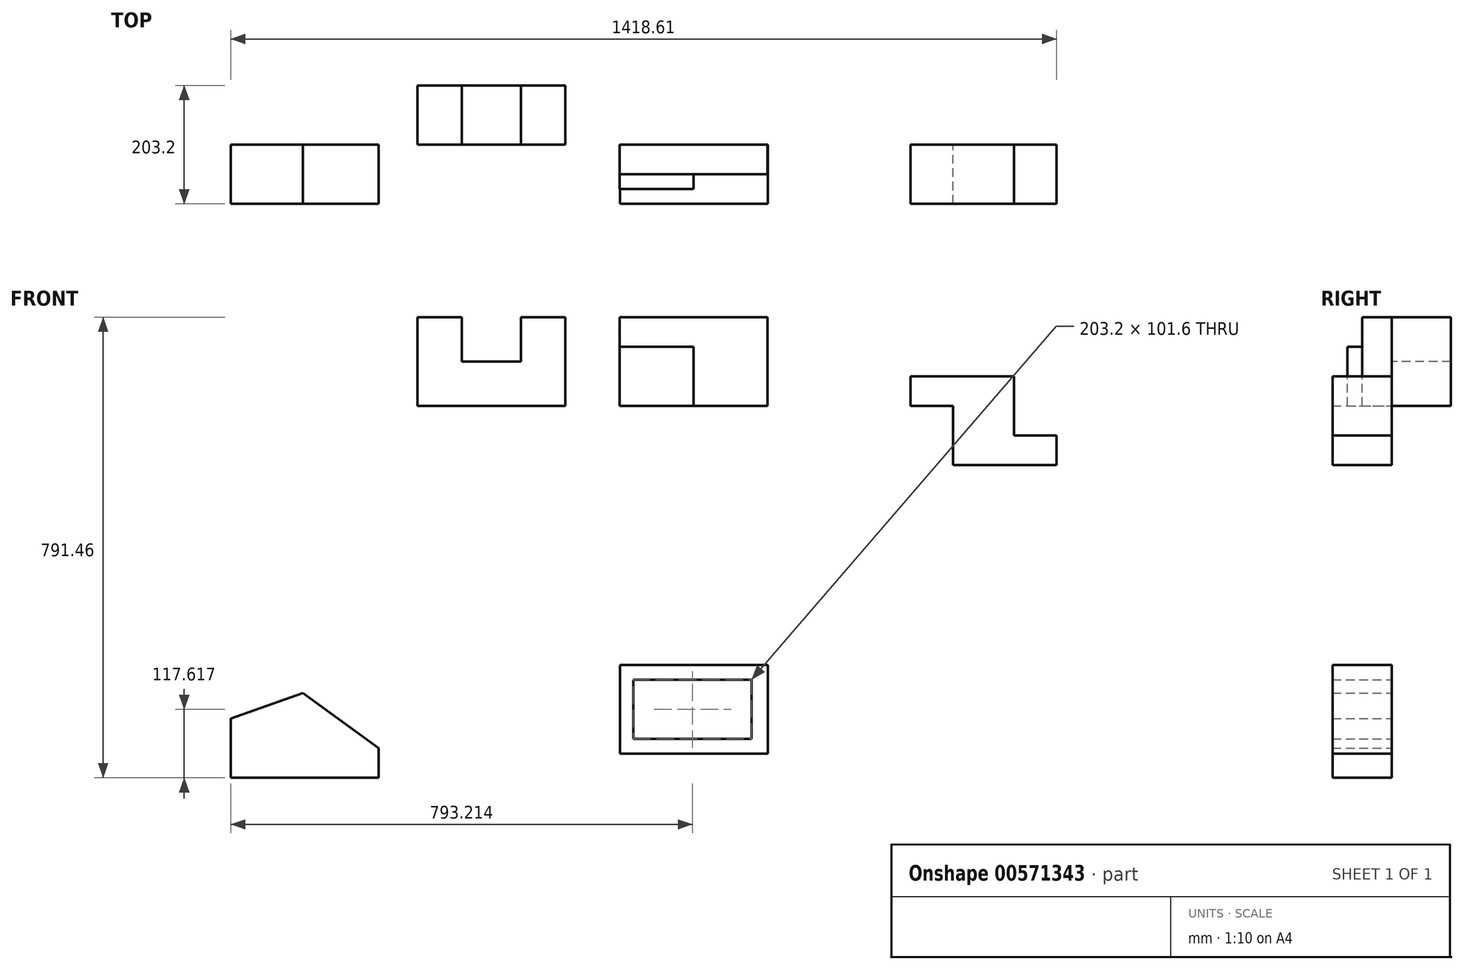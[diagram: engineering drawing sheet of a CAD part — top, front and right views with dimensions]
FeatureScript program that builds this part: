
annotation { "Feature Type Name" : "Feature", "Feature Type Description" : "" }
export const myFeature = defineFeature(function(context is Context, id is Id, definition is map)
    precondition{}
    {
        {
            var Q0;
            Q0=qCreatedBy(makeId("Front.planeOp"),FACE);
            var sketch = newSketch(context, id + "F0", { "sketchPlane" : qUnion([Q0])});
            skLineSegment(sketch, "E0", {"start": v(254, 152.4) * mm, "end": v(254, 0) * mm});
            skLineSegment(sketch, "E1", {"start": v(0, 0) * mm, "end": v(254, 0) * mm});
            skLineSegment(sketch, "E2", {"start": v(254, 152.4) * mm, "end": v(177.8, 152.4) * mm});
            skLineSegment(sketch, "E3", {"start": v(177.8, 76.2) * mm, "end": v(76.2, 76.2) * mm});
            skLineSegment(sketch, "E4", {"start": v(76.2, 76.2) * mm, "end": v(76.2, 152.4) * mm});
            skLineSegment(sketch, "E5", {"start": v(177.8, 76.2) * mm, "end": v(177.8, 152.4) * mm});
            skLineSegment(sketch, "E6", {"start": v(76.2, 152.4) * mm, "end": v(0, 152.4) * mm});
            skLineSegment(sketch, "E7", {"start": v(0, 0) * mm, "end": v(0, 152.4) * mm});
            skSolve(sketch);
        }
        {
            var Q0;
            Q0=makeQuery(id+"F0.imprint","IMPRINT",FACE,{"disambiguationData":[TD([[makeQuery(id+"F0.imprint","IMPRINT",EDGE,{"derivedFrom":sQuery(id+"F0.wireOp",EDGE,"E0")}),-1.0]])]});
            extrude(context, id + "F1", {"entities" : qUnion([Q0]), "oppositeDirection" : true, "depth" : 101.6 * mm, "offsetDistance" : 25.4 * mm});
        }
        {
            var Q0;
            Q0=qCreatedBy(makeId("Front.planeOp"),FACE);
            var sketch = newSketch(context, id + "F2", { "sketchPlane" : qUnion([Q0])});
            skLineSegment(sketch, "E8.bottom", {"start": v(601.12, 0) * mm, "end": v(347.12, 0) * mm});
            skLineSegment(sketch, "E8.top", {"start": v(601.12, 152.4) * mm, "end": v(347.12, 152.4) * mm});
            skLineSegment(sketch, "E8.left", {"start": v(601.12, 0) * mm, "end": v(601.12, 152.4) * mm});
            skLineSegment(sketch, "E8.right", {"start": v(347.12, 0) * mm, "end": v(347.12, 152.4) * mm});
            skSolve(sketch);
        }
        {
            var Q0;
            Q0 = qSketchRegion(id + "F2", true);
            extrude(context, id + "F3", {"entities" : qUnion([Q0]), "depth" : 101.6 * mm, "offsetDistance" : 25.4 * mm});
        }
        {
            var Q0;
            Q0=makeQuery(id+"F3.opExtrude","SWEPT_FACE",FACE,{"disambiguationData":[OSD([sQuery(id+"F2.wireOp",EDGE,"E8.top")])]});
            var sketch = newSketch(context, id + "F4", { "sketchPlane" : qUnion([Q0])});
            skLineSegment(sketch, "E9.bottom", {"start": v(601.12, -101.6) * mm, "end": v(474.12, -101.6) * mm});
            skLineSegment(sketch, "E9.top", {"start": v(601.12, -50.8) * mm, "end": v(474.12, -50.8) * mm});
            skLineSegment(sketch, "E9.left", {"start": v(601.12, -101.6) * mm, "end": v(601.12, -50.8) * mm});
            skLineSegment(sketch, "E9.right", {"start": v(474.12, -101.6) * mm, "end": v(474.12, -50.8) * mm});
            skSolve(sketch);
        }
        {
            var Q0;
            Q0=makeQuery(id+"F4.imprint","IMPRINT",FACE,{"disambiguationData":[TD([[makeQuery(id+"F4.imprint","IMPRINT",EDGE,{"derivedFrom":sQuery(id+"F4.wireOp",EDGE,"E9.bottom")}),-1.0]])]});
            extrude(context, id + "F5", {"entities" : qUnion([Q0]), "operationType" : NewBodyOperationType.REMOVE, "oppositeDirection" : true, "depth" : 152.4 * mm, "offsetDistance" : 25.4 * mm});
        }
        {
            var Q0;
            Q0=makeQuery(id+"F3.opExtrude","CAP_FACE",FACE,{"disambiguationData":[OSD([sQuery(id+"F2.wireOp",EDGE,"E8.bottom"),sQuery(id+"F2.wireOp",EDGE,"E8.top"),sQuery(id+"F2.wireOp",EDGE,"E8.left"),sQuery(id+"F2.wireOp",EDGE,"E8.right")])],"isStart":false});
            var sketch = newSketch(context, id + "F6", { "sketchPlane" : qUnion([Q0])});
            skLineSegment(sketch, "E10.bottom", {"start": v(347.12, 152.4) * mm, "end": v(474.12, 152.4) * mm});
            skLineSegment(sketch, "E10.top", {"start": v(347.12, 50.8) * mm, "end": v(474.12, 50.8) * mm});
            skLineSegment(sketch, "E10.left", {"start": v(347.12, 152.4) * mm, "end": v(347.12, 50.8) * mm});
            skLineSegment(sketch, "E10.right", {"start": v(474.12, 152.4) * mm, "end": v(474.12, 50.8) * mm});
            skSolve(sketch);
        }
        {
            var Q0;
            Q0=makeQuery(id+"F6.imprint","IMPRINT",FACE,{"disambiguationData":[TD([[makeQuery(id+"F6.imprint","IMPRINT",EDGE,{"derivedFrom":sQuery(id+"F6.wireOp",EDGE,"E10.bottom")}),1.0]])]});
            extrude(context, id + "F7", {"entities" : qUnion([Q0]), "operationType" : NewBodyOperationType.REMOVE, "oppositeDirection" : true, "depth" : 25.4 * mm, "offsetDistance" : 25.4 * mm});
        }
        {
            var Q0;
            Q0=makeQuery(id+"F7.boolean.opBoolean","COPY",FACE,{"derivedFrom":makeQuery(id+"F7.opExtrude","SWEPT_FACE",FACE,{"disambiguationData":[OSD([sQuery(id+"F6.wireOp",EDGE,"E10.top")])]})});
            extrude(context, id + "F8", {"entities" : qUnion([Q0]), "operationType" : NewBodyOperationType.ADD, "depth" : 50.8 * mm, "offsetDistance" : 25.4 * mm});
        }
        {
            var Q0;
            Q0=makeQuery(id+"F8.opExtrude","CAP_FACE",FACE,{"disambiguationData":[OSD([sQuery(id+"F6.wireOp",EDGE,"E10.top")])],"isStart":false});
            extrude(context, id + "F9", {"entities" : qUnion([Q0]), "operationType" : NewBodyOperationType.REMOVE, "oppositeDirection" : true, "depth" : 25.4 * mm, "offsetDistance" : 25.4 * mm});
        }
        {
            var Q0;
            Q0=makeQuery(id+"F9.boolean.opBoolean","COPY",FACE,{"derivedFrom":makeQuery(id+"F9.opExtrude","CAP_FACE",FACE,{"disambiguationData":[OSD([sQuery(id+"F6.wireOp",EDGE,"E10.top")])],"isStart":false})});
            extrude(context, id + "F10", {"entities" : qUnion([Q0]), "operationType" : NewBodyOperationType.REMOVE, "oppositeDirection" : true, "depth" : 76.2 * mm, "offsetDistance" : 25.4 * mm});
        }
        {
            var Q0;
            Q0=makeQuery(id+"F3.opExtrude","SWEPT_FACE",FACE,{"disambiguationData":[OSD([sQuery(id+"F2.wireOp",EDGE,"E8.top")])]});
            var sketch = newSketch(context, id + "F11", { "sketchPlane" : qUnion([Q0])});
            skLineSegment(sketch, "E11.bottom", {"start": v(474.12, -50.8) * mm, "end": v(347.12, -50.8) * mm});
            skLineSegment(sketch, "E11.top", {"start": v(474.12, -76.2) * mm, "end": v(347.12, -76.2) * mm});
            skLineSegment(sketch, "E11.left", {"start": v(474.12, -50.8) * mm, "end": v(474.12, -76.2) * mm});
            skLineSegment(sketch, "E11.right", {"start": v(347.12, -50.8) * mm, "end": v(347.12, -76.2) * mm});
            skSolve(sketch);
        }
        {
            var Q0;
            Q0 = qSketchRegion(id + "F11", true);
            extrude(context, id + "F12", {"entities" : qUnion([Q0]), "operationType" : NewBodyOperationType.REMOVE, "oppositeDirection" : true, "depth" : 50.8 * mm, "offsetDistance" : 25.4 * mm});
        }
        {
            var Q0;
            Q0=qCreatedBy(makeId("Front.planeOp"),FACE);
            var sketch = newSketch(context, id + "F13", { "sketchPlane" : qUnion([Q0])});
            skLineSegment(sketch, "E12", {"start": v(1097.77, -101.6) * mm, "end": v(1097.77, -50.8) * mm});
            skLineSegment(sketch, "E13", {"start": v(919.97, -101.56) * mm, "end": v(1097.77, -101.6) * mm});
            skLineSegment(sketch, "E14", {"start": v(1097.77, -50.8) * mm, "end": v(1024.56, -50.8) * mm});
            skLineSegment(sketch, "E15", {"start": v(1024.56, -50.8) * mm, "end": v(1024.56, 50.8) * mm});
            skLineSegment(sketch, "E16", {"start": v(1024.56, 50.8) * mm, "end": v(846.76, 50.8) * mm});
            skLineSegment(sketch, "E17", {"start": v(846.76, 50.8) * mm, "end": v(846.76, 0) * mm});
            skLineSegment(sketch, "E18", {"start": v(919.97, -101.56) * mm, "end": v(919.97, 0) * mm});
            skLineSegment(sketch, "E19", {"start": v(846.76, 0) * mm, "end": v(919.97, 0) * mm});
            skSolve(sketch);
        }
        {
            var Q0;
            Q0 = qSketchRegion(id + "F13", true);
            extrude(context, id + "F14", {"entities" : qUnion([Q0]), "depth" : 101.6 * mm, "offsetDistance" : 25.4 * mm});
        }
        {
            var Q0;
            Q0=qCreatedBy(makeId("Front.planeOp"),FACE);
            var sketch = newSketch(context, id + "F15", { "sketchPlane" : qUnion([Q0])});
            skLineSegment(sketch, "E20", {"start": v(-66.84, -639.06) * mm, "end": v(-66.84, -588.26) * mm});
            skLineSegment(sketch, "E21", {"start": v(-320.84, -537.46) * mm, "end": v(-320.84, -639.06) * mm});
            skLineSegment(sketch, "E22", {"start": v(-66.84, -639.06) * mm, "end": v(-320.84, -639.06) * mm});
            skLineSegment(sketch, "E23", {"start": v(-320.84, -537.46) * mm, "end": v(-197.2, -493.3) * mm});
            skLineSegment(sketch, "E24", {"start": v(-197.2, -493.3) * mm, "end": v(-66.84, -588.26) * mm});
            skSolve(sketch);
        }
        {
            var Q0;
            Q0 = qSketchRegion(id + "F15", true);
            extrude(context, id + "F16", {"entities" : qUnion([Q0]), "depth" : 101.6 * mm, "offsetDistance" : 25.4 * mm});
        }
        {
            var Q0;
            Q0=qCreatedBy(makeId("Front.planeOp"),FACE);
            var sketch = newSketch(context, id + "F17", { "sketchPlane" : qUnion([Q0])});
            skLineSegment(sketch, "E25", {"start": v(602.16, -597.64) * mm, "end": v(602.16, -445.24) * mm});
            skLineSegment(sketch, "E26", {"start": v(602.16, -445.24) * mm, "end": v(348.16, -445.24) * mm});
            skLineSegment(sketch, "E27", {"start": v(348.16, -445.24) * mm, "end": v(348.16, -597.64) * mm});
            skLineSegment(sketch, "E28", {"start": v(348.16, -597.64) * mm, "end": v(602.16, -597.64) * mm});
            skLineSegment(sketch, "E29", {"start": v(370.77, -572.24) * mm, "end": v(370.77, -470.64) * mm});
            skLineSegment(sketch, "E30", {"start": v(370.77, -470.64) * mm, "end": v(573.97, -470.64) * mm});
            skLineSegment(sketch, "E31", {"start": v(573.97, -470.64) * mm, "end": v(573.97, -572.24) * mm});
            skLineSegment(sketch, "E32", {"start": v(370.77, -572.24) * mm, "end": v(573.97, -572.24) * mm});
            skSolve(sketch);
        }
        {
            var Q0;
            Q0 = qSketchRegion(id + "F17", true);
            extrude(context, id + "F18", {"entities" : qUnion([Q0]), "depth" : 101.6 * mm, "offsetDistance" : 25.4 * mm});
        }
    });
